# Revit family: NEOREST WX2_TEU
name_source: partatom
category: Plumbing Fixtures
revit_build: Autodesk Revit 2018 (Build: 20170223_1515(x64)
units: mm (PartAtom-declared; Revit-internal decimal feet)

## family parameters
Always vertical = Yes
Cut with Voids When Loaded = No
OmniClass Number = 23.45.00.00
OmniClass Title = Sanitary, Laundry, and Cleaning Equipment
Part Type = Normal
Room Calculation Point = No
Round Connector Dimension = Use Diameter
Shared = No
Work Plane-Based = No

## types (1)
- NEOREST WX2_TEU
    CW Connection = Yes
    Description = NEOREST WX2
    Finish = White
    HW Connection = No
    Height = 447 mm
    Length = 675 mm  [stored 2.21457 ft]
    Manufacturer = TOTO LTD.
    Material 1 = Ceramic
    Material 2 = Plastic
    Model = TCF95280GEU(WASHLET, ACTILIGHT technology)
    OPTIONAL ACCESORY = Push plate：MB177EM#S/Water Connection set: HM183
    REQUIRED ACCESSORY = WC（wall-hung,AC）：CW928PZY/CONCEALED CISTERNS：WH182EAT
    Rough-in = 0 mm  [stored 0 ft]
    Seat Included = Yes
    URL = https://eu.toto.com
    Vent Connection = No
    Voltage = 220–240 V/50 Hz
    Waste Connection = Yes
    Water Pressure = FP0.05MPa～SP1.0MPa
    Water Use = 4.5L/3L　6.0/3L（England）
    Width = 449 mm  [stored 1.4731 ft]

note: [stored X ft] marks values corroborated as IEEE doubles in the binary element streams (Revit-internal decimal feet)

## geometry (parser evidence)
native form markers: Sweep x2
no freeform markers — native parametric forms only
